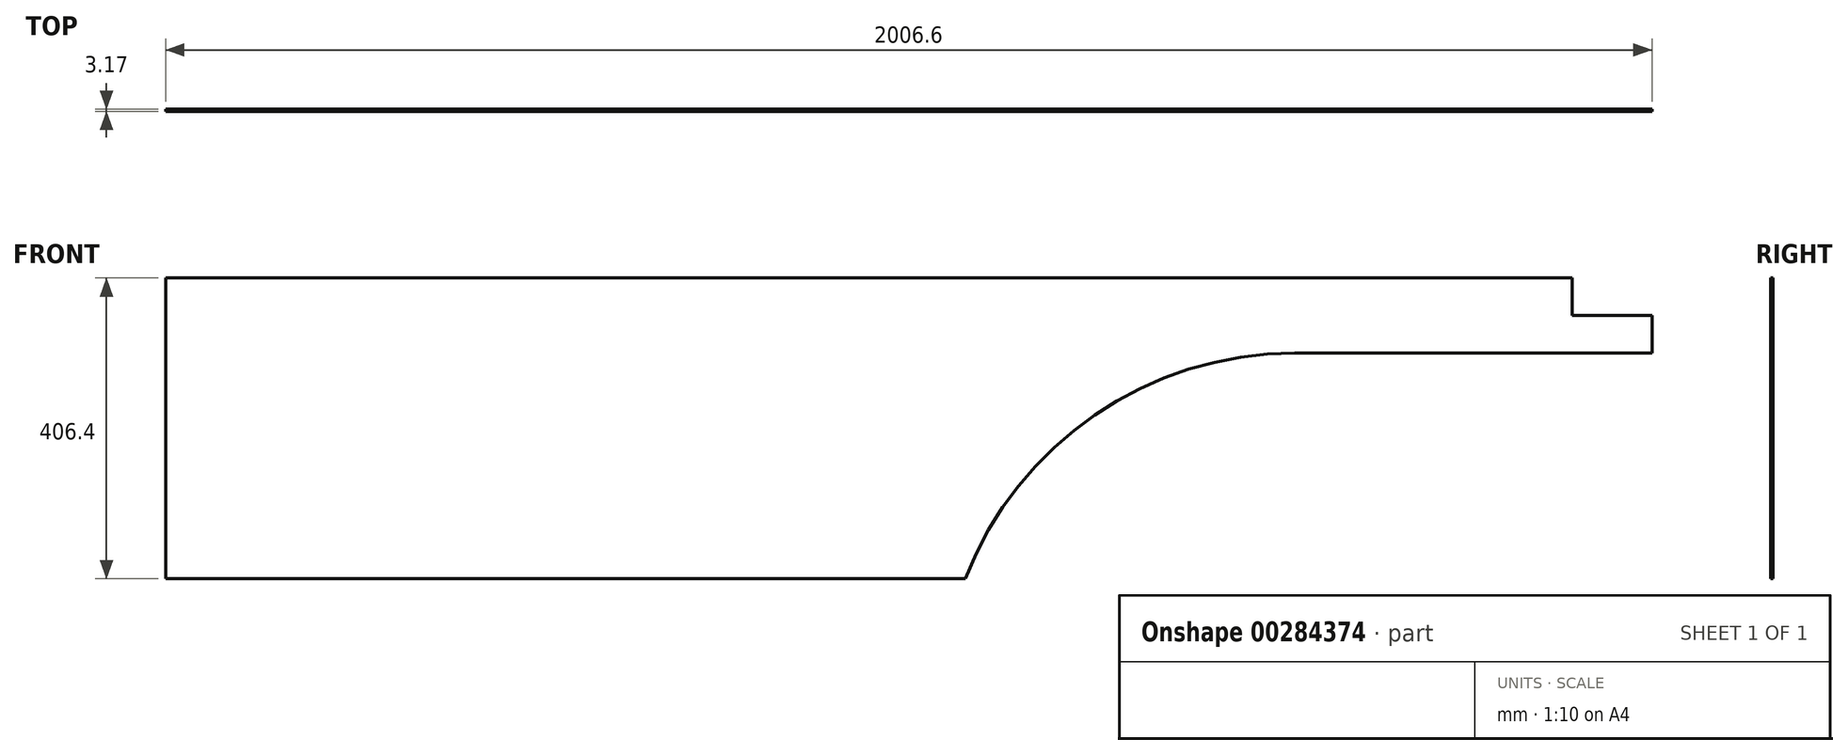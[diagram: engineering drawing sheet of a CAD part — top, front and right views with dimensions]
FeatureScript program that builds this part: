
annotation { "Feature Type Name" : "Feature", "Feature Type Description" : "" }
export const myFeature = defineFeature(function(context is Context, id is Id, definition is map)
    precondition{}
    {
        {
            var Q0;
            Q0=qCreatedBy(makeId("Front.planeOp"),FACE);
            var sketch = newSketch(context, id + "F0", { "sketchPlane" : qUnion([Q0])});
            skLineSegment(sketch, "E0", {"start": v(0, 0) * mm, "end": v(0, 406.4) * mm});
            skLineSegment(sketch, "E1", {"start": v(0, 406.4) * mm, "end": v(1898.65, 406.4) * mm});
            skLineSegment(sketch, "E2", {"start": v(1898.65, 406.4) * mm, "end": v(1898.65, 355.6) * mm});
            skLineSegment(sketch, "E3", {"start": v(1898.65, 355.6) * mm, "end": v(2006.6, 355.6) * mm});
            skLineSegment(sketch, "E4", {"start": v(2006.6, 355.6) * mm, "end": v(2006.6, 304.8) * mm});
            skLineSegment(sketch, "E5", {"start": v(2006.6, 304.8) * mm, "end": v(1524, 304.8) * mm});
            skLineSegment(sketch, "E6", {"start": v(1079.5, 0) * mm, "end": v(0, 0) * mm});
            skArc(sketch, "E7", {"start": v(1524, 304.8) * mm, "mid": v(1254.52, 221.28) * mm, "end": v(1079.5, 0) * mm});
            skSolve(sketch);
        }
        {
            var Q0;
            Q0 = qSketchRegion(id + "F0", true);
            extrude(context, id + "F1", {"entities" : qUnion([Q0]), "depth" : 3.17 * mm});
        }
    });
